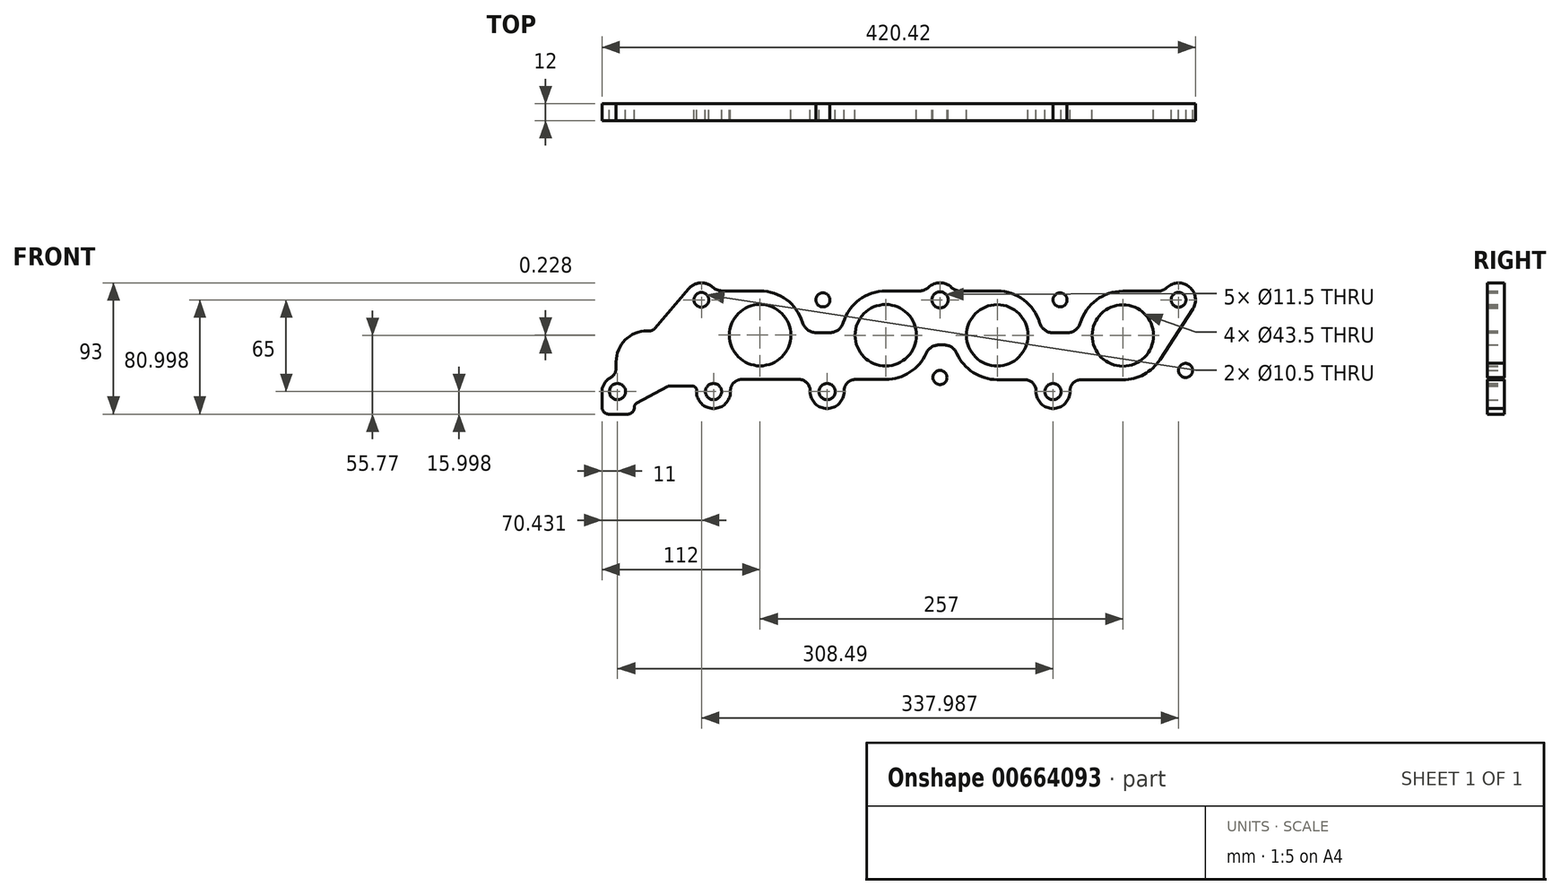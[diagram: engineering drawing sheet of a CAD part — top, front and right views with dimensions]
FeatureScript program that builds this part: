
annotation { "Feature Type Name" : "Feature", "Feature Type Description" : "" }
export const myFeature = defineFeature(function(context is Context, id is Id, definition is map)
    precondition{}
    {
        {
            var Q0;
            Q0=qCreatedBy(makeId("Front.planeOp"),FACE);
            var sketch = newSketch(context, id + "F0", { "sketchPlane" : qUnion([Q0]), "disableImprinting" : false});
            skLineSegment(sketch, "E0", {"start": v(-196.56, 14.9) * mm, "end": v(141.43, 14.9) * mm, "construction": true});
            skLineSegment(sketch, "E1", {"start": v(143.55, -50.1) * mm, "end": v(-255.99, -50.1) * mm, "construction": true});
            skCircle(sketch, "E2", {"center": v(-27.56, 14.9) * mm, "radius": 5.75 * mm});
            skCircle(sketch, "E3", {"center": v(141.43, 14.9) * mm, "radius": 5.25 * mm});
            skCircle(sketch, "E4", {"center": v(-196.56, 14.9) * mm, "radius": 5.25 * mm});
            skCircle(sketch, "E5", {"center": v(52.5, -50.1) * mm, "radius": 5.75 * mm});
            skCircle(sketch, "E6", {"center": v(-107.5, -50.1) * mm, "radius": 5.75 * mm});
            skCircle(sketch, "E7", {"center": v(-187.99, -50.1) * mm, "radius": 5.75 * mm});
            skCircle(sketch, "E8", {"center": v(-255.99, -50.1) * mm, "radius": 5.75 * mm});
            skCircle(sketch, "E9.converted", {"center": v(102.01, -10.32) * mm, "radius": 21.75 * mm});
            skCircle(sketch, "E10.converted", {"center": v(13.01, -10.24) * mm, "radius": 21.75 * mm});
            skCircle(sketch, "E11.converted", {"center": v(-154.99, -10.1) * mm, "radius": 21.75 * mm});
            skLineSegment(sketch, "E12", {"start": v(-154.99, -10.1) * mm, "end": v(102.01, -10.32) * mm, "construction": true});
            skCircle(sketch, "E13", {"center": v(-65.99, -10.17) * mm, "radius": 21.75 * mm});
            skLineSegment(sketch, "E14", {"start": v(-65.99, -10.17) * mm, "end": v(-65.99, 38.54) * mm, "construction": true});
            skArc(sketch, "E15.0", {"start": v(-124.95, -1.13) * mm, "mid": v(-136.24, 15.04) * mm, "end": v(-154.96, 21.26) * mm});
            skArc(sketch, "E16.0", {"start": v(-65.96, 21.18) * mm, "mid": v(-84.7, 15) * mm, "end": v(-96.02, -1.16) * mm});
            skArc(sketch, "E17.0", {"start": v(43.05, -1.28) * mm, "mid": v(31.76, 14.89) * mm, "end": v(13.04, 21.1) * mm});
            skArc(sketch, "E18.0", {"start": v(102.04, 21.03) * mm, "mid": v(83.3, 14.84) * mm, "end": v(71.98, -1.3) * mm});
            skLineSegment(sketch, "E19", {"start": v(-181.87, 21.28) * mm, "end": v(-154.96, 21.26) * mm});
            skLineSegment(sketch, "E20", {"start": v(13.01, -10.24) * mm, "end": v(13.06, 50.13) * mm, "construction": true});
            skLineSegment(sketch, "E21.trimOffspring", {"start": v(102.04, 21.03) * mm, "end": v(126.43, 21) * mm});
            skLineSegment(sketch, "E22.trimOffspring", {"start": v(-65.96, 21.18) * mm, "end": v(-42.4, 21.16) * mm});
            skLineSegment(sketch, "E23", {"start": v(101.98, -41.67) * mm, "end": v(72.5, -41.64) * mm});
            skLineSegment(sketch, "E24", {"start": v(-66.02, -41.52) * mm, "end": v(-87.5, -41.5) * mm});
            skLineSegment(sketch, "E25.0", {"start": v(-115.37, -8.28) * mm, "end": v(-105.6, -8.29) * mm});
            skLineSegment(sketch, "E26.trimOffspring", {"start": v(52.63, -8.43) * mm, "end": v(62.4, -8.43) * mm});
            skLineSegment(sketch, "E27.0", {"start": v(-24.76, -17.06) * mm, "end": v(-28.24, -17.05) * mm});
            skArc(sketch, "E28", {"start": v(-119.5, -50.1) * mm, "mid": v(-107.5, -62.1) * mm, "end": v(-95.5, -50.1) * mm});
            skArc(sketch, "E29", {"start": v(40.5, -50.1) * mm, "mid": v(52.5, -62.1) * mm, "end": v(64.5, -50.1) * mm});
            skArc(sketch, "E30", {"start": v(-19.45, 23.76) * mm, "mid": v(-27.55, 26.9) * mm, "end": v(-35.65, 23.77) * mm});
            skArc(sketch, "E31", {"start": v(151.5, 8.38) * mm, "mid": v(149.14, 24.1) * mm, "end": v(133.25, 23.7) * mm});
            skArc(sketch, "E32", {"start": v(-188.54, 23.84) * mm, "mid": v(-197.37, 26.88) * mm, "end": v(-205.7, 22.68) * mm});
            skArc(sketch, "E33", {"start": v(-199.99, -50.1) * mm, "mid": v(-187.99, -62.1) * mm, "end": v(-175.99, -50.1) * mm});
            skLineSegment(sketch, "E34", {"start": v(40.5, -50.1) * mm, "end": v(40.5, -49.6) * mm});
            skLineSegment(sketch, "E35", {"start": v(64.5, -50.1) * mm, "end": v(64.5, -49.64) * mm});
            skLineSegment(sketch, "E36", {"start": v(-95.5, -50.1) * mm, "end": v(-95.5, -49.5) * mm});
            skLineSegment(sketch, "E37", {"start": v(-119.5, -50.1) * mm, "end": v(-119.5, -49.47) * mm});
            skLineSegment(sketch, "E38", {"start": v(128.31, -27.38) * mm, "end": v(151.5, 8.38) * mm});
            skArc(sketch, "E39.trimOffspring", {"start": v(101.98, -41.67) * mm, "mid": v(116.97, -37.87) * mm, "end": v(128.31, -27.38) * mm});
            skLineSegment(sketch, "E40.trimOffspring", {"start": v(32.5, -41.6) * mm, "end": v(12.98, -41.6) * mm});
            skArc(sketch, "E41.trimOffspring", {"start": v(-15.63, -23) * mm, "mid": v(-4.08, -36.53) * mm, "end": v(12.98, -41.6) * mm});
            skLineSegment(sketch, "E42.trimOffspring", {"start": v(-12.7, 21.13) * mm, "end": v(13.04, 21.1) * mm});
            skArc(sketch, "E43.trimOffspring", {"start": v(-66.02, -41.52) * mm, "mid": v(-48.95, -36.49) * mm, "end": v(-37.37, -22.97) * mm});
            skLineSegment(sketch, "E44.trimOffspring", {"start": v(-127.5, -41.47) * mm, "end": v(-167.98, -41.43) * mm});
            skLineSegment(sketch, "E45", {"start": v(-175.99, -50.1) * mm, "end": v(-175.99, -49.43) * mm});
            skLineSegment(sketch, "E46", {"start": v(52.5, 14.9) * mm, "end": v(52.5, -85.6) * mm, "construction": true});
            skLineSegment(sketch, "E47.trimOffspring", {"start": v(-202.99, -46.1) * mm, "end": v(-219.23, -46.1) * mm});
            skLineSegment(sketch, "E48", {"start": v(-187.99, -50.1) * mm, "end": v(-187.99, -86.68) * mm});
            skLineSegment(sketch, "E49.0", {"start": v(-243.99, -60.88) * mm, "end": v(-243.99, -61.1) * mm});
            skLineSegment(sketch, "E50.trimOffspring", {"start": v(-248.99, -66.1) * mm, "end": v(-261.99, -66.1) * mm});
            skLineSegment(sketch, "E51", {"start": v(-199.99, -50.1) * mm, "end": v(-199.99, -49.1) * mm});
            skLineSegment(sketch, "E52.0", {"start": v(-266.99, -50.1) * mm, "end": v(-266.99, -61.1) * mm});
            skArc(sketch, "E53", {"start": v(-261.2, -40.4) * mm, "mid": v(-265.43, -44.45) * mm, "end": v(-266.99, -50.1) * mm});
            skLineSegment(sketch, "E54.0", {"start": v(-233.3, -7.1) * mm, "end": v(-234.99, -7.1) * mm});
            skArc(sketch, "E55", {"start": v(-234.99, -7.1) * mm, "mid": v(-250.55, -13.54) * mm, "end": v(-256.99, -29.1) * mm});
            skLineSegment(sketch, "E56.trimOffspring", {"start": v(-256.99, -29.1) * mm, "end": v(-256.99, -33.36) * mm});
            skLineSegment(sketch, "E57", {"start": v(-229.5, -5.33) * mm, "end": v(-205.7, 22.68) * mm});
            skLineSegment(sketch, "E58", {"start": v(-220.66, -46.45) * mm, "end": v(-242.42, -58.24) * mm});
            skPoint(sketch, "E59.0.visualSharp", {"position": v(-266.99, -66.1) * mm});
            skArc(sketch, "E59.0.filletArc", {"start": v(-266.99, -61.1) * mm, "mid": v(-265.53, -64.63) * mm, "end": v(-261.99, -66.1) * mm});
            skPoint(sketch, "E60.0.visualSharp", {"position": v(-243.99, -66.1) * mm});
            skArc(sketch, "E60.0.filletArc", {"start": v(-248.99, -66.1) * mm, "mid": v(-245.45, -64.63) * mm, "end": v(-243.99, -61.1) * mm});
            skPoint(sketch, "E61.0.visualSharp", {"position": v(-199.99, -46.1) * mm});
            skArc(sketch, "E61.0.filletArc", {"start": v(-199.99, -49.1) * mm, "mid": v(-200.87, -46.97) * mm, "end": v(-202.99, -46.1) * mm});
            skPoint(sketch, "E62.0.visualSharp", {"position": v(-219.99, -46.1) * mm});
            skArc(sketch, "E62.0.filletArc", {"start": v(-219.23, -46.1) * mm, "mid": v(-219.97, -46.18) * mm, "end": v(-220.66, -46.45) * mm});
            skPoint(sketch, "E63.0.visualSharp", {"position": v(-243.99, -59.1) * mm});
            skArc(sketch, "E63.0.filletArc", {"start": v(-242.42, -58.24) * mm, "mid": v(-243.57, -59.34) * mm, "end": v(-243.99, -60.88) * mm});
            skPoint(sketch, "E64.0.visualSharp", {"position": v(-256.99, -39.14) * mm});
            skArc(sketch, "E64.0.filletArc", {"start": v(-261.2, -40.4) * mm, "mid": v(-258.12, -37.46) * mm, "end": v(-256.99, -33.36) * mm});
            skPoint(sketch, "E65.0.visualSharp", {"position": v(-230.99, -7.1) * mm});
            skArc(sketch, "E65.0.filletArc", {"start": v(-233.3, -7.1) * mm, "mid": v(-231.2, -6.63) * mm, "end": v(-229.5, -5.33) * mm});
            skPoint(sketch, "E66.0.visualSharp", {"position": v(-186.4, 21.29) * mm});
            skArc(sketch, "E66.0.filletArc", {"start": v(-188.54, 23.84) * mm, "mid": v(-185.45, 21.95) * mm, "end": v(-181.87, 21.28) * mm});
            skArc(sketch, "E67.0.filletArc", {"start": v(-124.95, -1.13) * mm, "mid": v(-121.34, -6.3) * mm, "end": v(-115.37, -8.28) * mm});
            skPoint(sketch, "E68.0.visualSharp", {"position": v(-97.28, -8.3) * mm});
            skArc(sketch, "E68.0.filletArc", {"start": v(-105.6, -8.29) * mm, "mid": v(-99.63, -6.31) * mm, "end": v(-96.02, -1.16) * mm});
            skPoint(sketch, "E69.0.visualSharp", {"position": v(-37.8, 21.15) * mm});
            skArc(sketch, "E69.0.filletArc", {"start": v(-42.4, 21.16) * mm, "mid": v(-38.78, 21.83) * mm, "end": v(-35.65, 23.77) * mm});
            skPoint(sketch, "E70.0.visualSharp", {"position": v(-17.3, 21.14) * mm});
            skArc(sketch, "E70.0.filletArc", {"start": v(-19.45, 23.76) * mm, "mid": v(-16.33, 21.81) * mm, "end": v(-12.7, 21.13) * mm});
            skPoint(sketch, "E71.0.visualSharp", {"position": v(44.3, -8.42) * mm});
            skArc(sketch, "E71.0.filletArc", {"start": v(43.05, -1.28) * mm, "mid": v(46.66, -6.44) * mm, "end": v(52.63, -8.43) * mm});
            skPoint(sketch, "E72.0.visualSharp", {"position": v(70.72, -8.44) * mm});
            skArc(sketch, "E72.0.filletArc", {"start": v(62.4, -8.43) * mm, "mid": v(68.37, -6.46) * mm, "end": v(71.98, -1.3) * mm});
            skPoint(sketch, "E73.0.visualSharp", {"position": v(131.1, 21) * mm});
            skArc(sketch, "E73.0.filletArc", {"start": v(126.43, 21) * mm, "mid": v(130.1, 21.7) * mm, "end": v(133.25, 23.7) * mm});
            skPoint(sketch, "E74.0.visualSharp", {"position": v(-17.59, -17.06) * mm});
            skArc(sketch, "E74.0.filletArc", {"start": v(-15.63, -23) * mm, "mid": v(-19.32, -18.67) * mm, "end": v(-24.76, -17.06) * mm});
            skPoint(sketch, "E75.0.visualSharp", {"position": v(-35.4, -17.05) * mm});
            skArc(sketch, "E75.0.filletArc", {"start": v(-28.24, -17.05) * mm, "mid": v(-33.68, -18.66) * mm, "end": v(-37.37, -22.97) * mm});
            skPoint(sketch, "E76.0.visualSharp", {"position": v(-175.99, -41.42) * mm});
            skArc(sketch, "E76.0.filletArc", {"start": v(-167.98, -41.43) * mm, "mid": v(-173.64, -43.77) * mm, "end": v(-175.99, -49.43) * mm});
            skPoint(sketch, "E77.0.visualSharp", {"position": v(-119.5, -41.47) * mm});
            skArc(sketch, "E77.0.filletArc", {"start": v(-119.5, -49.47) * mm, "mid": v(-121.84, -43.81) * mm, "end": v(-127.5, -41.47) * mm});
            skPoint(sketch, "E78.0.visualSharp", {"position": v(-95.5, -41.5) * mm});
            skArc(sketch, "E78.0.filletArc", {"start": v(-87.5, -41.5) * mm, "mid": v(-93.15, -43.84) * mm, "end": v(-95.5, -49.5) * mm});
            skPoint(sketch, "E79.0.visualSharp", {"position": v(40.5, -41.62) * mm});
            skArc(sketch, "E79.0.filletArc", {"start": v(40.5, -49.6) * mm, "mid": v(38.16, -43.95) * mm, "end": v(32.5, -41.6) * mm});
            skPoint(sketch, "E80.0.newPointA", {"position": v(64.5, -41.62) * mm});
            skArc(sketch, "E80.0.filletArc", {"start": v(72.5, -41.64) * mm, "mid": v(66.85, -43.98) * mm, "end": v(64.5, -49.64) * mm});
            skLineSegment(sketch, "E81", {"start": v(-107.5, -62.1) * mm, "end": v(-187.99, -62.1) * mm, "construction": true});
            skLineSegment(sketch, "E82.0", {"start": v(143.55, -40.1) * mm, "end": v(-255.99, -40.1) * mm, "construction": true});
            skLineSegment(sketch, "E83", {"start": v(-27.56, 14.9) * mm, "end": v(-27.56, -50.1) * mm, "construction": true});
            skCircle(sketch, "E84", {"center": v(-27.56, -40.1) * mm, "radius": 5 * mm});
            skLineSegment(sketch, "E85", {"start": v(141.43, 14.9) * mm, "end": v(141.43, -46.5) * mm, "construction": true});
            skLineSegment(sketch, "E86.0", {"start": v(146.43, 14.9) * mm, "end": v(146.43, -46.5) * mm, "construction": true});
            skLineSegment(sketch, "E87.0", {"start": v(146.43, -35.1) * mm, "end": v(-255.99, -35.1) * mm, "construction": true});
            skCircle(sketch, "E88", {"center": v(146.43, -35.1) * mm, "radius": 5 * mm});
            skLineSegment(sketch, "E89.0", {"start": v(57.5, 14.9) * mm, "end": v(57.5, -85.6) * mm, "construction": true});
            skCircle(sketch, "E90", {"center": v(57.5, 14.9) * mm, "radius": 5 * mm});
            skLineSegment(sketch, "E91", {"start": v(-107.5, -50.1) * mm, "end": v(-107.5, 43.3) * mm, "construction": true});
            skLineSegment(sketch, "E92.0", {"start": v(-110.5, -50.1) * mm, "end": v(-110.5, 43.3) * mm, "construction": true});
            skCircle(sketch, "E93", {"center": v(-110.5, 14.9) * mm, "radius": 5 * mm});
            skSolve(sketch);
        }
        {
            var Q0;
            Q0 = qSketchRegion(id + "F0", true);
            extrude(context, id + "F1", {"entities" : qUnion([Q0]), "flatOperationType" : FlatOperationType.REMOVE, "depth" : 12 * mm, "offsetDistance" : 25 * mm, "domain" : OperationDomain.MODEL});
        }
    });
